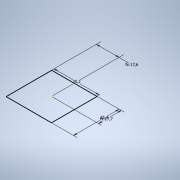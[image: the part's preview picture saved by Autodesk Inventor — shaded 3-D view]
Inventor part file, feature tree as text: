
AUTODESK INVENTOR PART (.ipt)
format: ipt  version: 2020.2 (Build 242310000, 310)  size: 89,600 bytes
history: native  units: mm
features: sketch x1
ambient origin geometry x8: Origin, YZ Plane, XZ Plane, XY Plane, X Axis, Y Axis, Z Axis, Center Point
feature tree (1):
  sketch  "Sketch1"  dims[d0=35.2mm d1=35.4mm d2=17.7mm d3=17.6mm]
